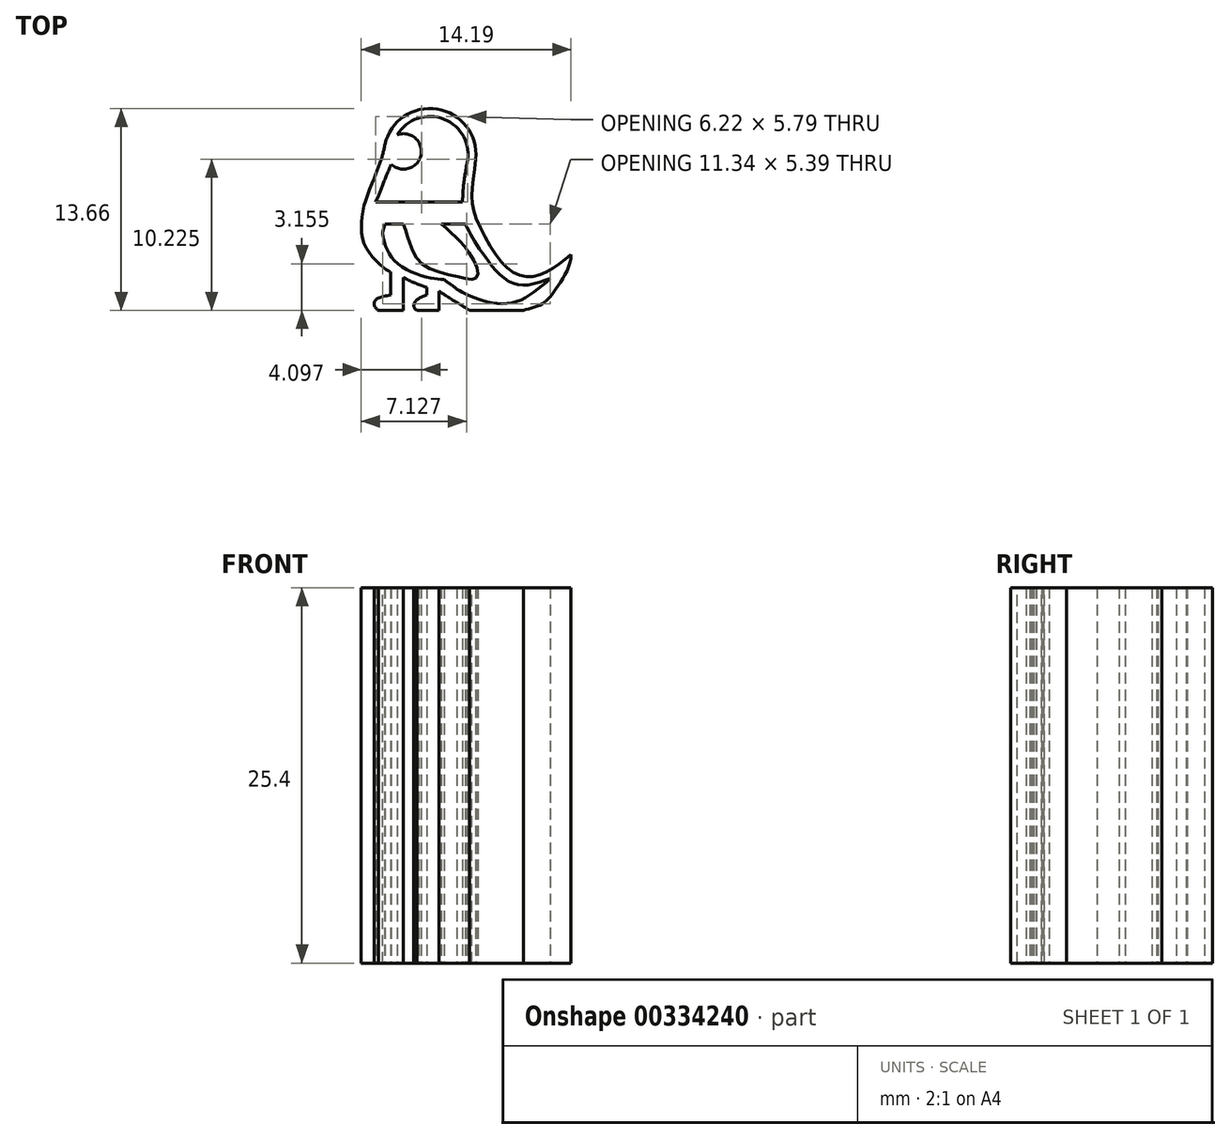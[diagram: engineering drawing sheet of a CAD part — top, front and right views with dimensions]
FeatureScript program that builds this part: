
annotation { "Feature Type Name" : "Feature", "Feature Type Description" : "" }
export const myFeature = defineFeature(function(context is Context, id is Id, definition is map)
    precondition{}
    {
        {
            var Q0;
            Q0=qCreatedBy(makeId("Top.planeOp"),FACE);
            var sketch = newSketch(context, id + "F0", { "sketchPlane" : qUnion([Q0])});
            skArc(sketch, "E0", {"start": v(-20.34, 35.83) * mm, "mid": v(-22.96, 39.22) * mm, "end": v(-26.5, 36.8) * mm});
            skLineSegment(sketch, "E1.left", {"start": v(-26.1, 28.2) * mm, "end": v(-26.1, 26.63) * mm});
            skLineSegment(sketch, "E1.right", {"start": v(-25.25, 27.82) * mm, "end": v(-25.25, 26.63) * mm});
            skFitSpline(sketch, "E2", {"points": [v(-26.1, 26.63) * mm, v(-27.1, 26.32) * mm, v(-27.2, 25.9) * mm, v(-26.93, 25.6) * mm], "startDerivative": vector(-2.75, -0.43) * mm, "endDerivative": vector(1.25, -0.98) * mm});
            skFitSpline(sketch, "E3", {"points": [v(-25.25, 26.63) * mm, v(-25.25, 25.77) * mm], "startDerivative": vector(0, -0.86) * mm, "endDerivative": vector(0, -0.86) * mm});
            skLineSegment(sketch, "E4", {"start": v(-26.93, 25.6) * mm, "end": v(-25.25, 25.6) * mm});
            skLineSegment(sketch, "E5", {"start": v(-25.25, 25.77) * mm, "end": v(-25.25, 25.6) * mm});
            skFitSpline(sketch, "E6", {"points": [v(-25.25, 27.82) * mm, v(-24.64, 27.52) * mm, v(-24.18, 27.33) * mm], "startDerivative": vector(1.23, -0.6) * mm, "endDerivative": vector(0.89, -0.38) * mm});
            skFitSpline(sketch, "E7", {"points": [v(-24.18, 27.33) * mm, v(-23.67, 27.16) * mm], "startDerivative": vector(0.51, -0.17) * mm, "endDerivative": vector(0.51, -0.17) * mm});
            skLineSegment(sketch, "E8.left", {"start": v(-23.67, 27.16) * mm, "end": v(-23.67, 26.63) * mm});
            skLineSegment(sketch, "E8.right", {"start": v(-22.82, 26.9) * mm, "end": v(-22.82, 26.63) * mm});
            skFitSpline(sketch, "E9", {"points": [v(-23.67, 26.63) * mm, v(-24.18, 26.4) * mm, v(-24.48, 26.12) * mm, v(-24.51, 25.8) * mm, v(-24.32, 25.6) * mm], "startDerivative": vector(-1.8, -0.7) * mm, "endDerivative": vector(1.18, -0.76) * mm});
            skLineSegment(sketch, "E10", {"start": v(-24.32, 25.6) * mm, "end": v(-22.82, 25.6) * mm});
            skLineSegment(sketch, "E11", {"start": v(-22.82, 26.63) * mm, "end": v(-22.82, 25.6) * mm});
            skLineSegment(sketch, "E12", {"start": v(-26.5, 36.8) * mm, "end": v(-30.17, 36.8) * mm});
            skLineSegment(sketch, "E13", {"start": v(-30.17, 36.8) * mm, "end": v(-27.08, 34.89) * mm});
            skFitSpline(sketch, "E14.trimOffspring", {"points": [v(-26.5, 36.8) * mm, v(-27.79, 33.03) * mm, v(-27.66, 29.66) * mm, v(-26.14, 28.2) * mm, v(-26.1, 28.2) * mm], "startDerivative": vector(-1.27, -9.96) * mm, "endDerivative": vector(0.77, 0.4) * mm});
            skArc(sketch, "E15", {"start": v(-20.93, 35.55) * mm, "mid": v(-22.48, 38.52) * mm, "end": v(-25.65, 37.46) * mm});
            skPoint(sketch, "E16.orphan", {"position": v(-22.82, 27.2) * mm});
            skFitSpline(sketch, "E17", {"points": [v(-20.93, 35.55) * mm, v(-21.22, 33.37) * mm, v(-20.95, 31.12) * mm, v(-19.9, 28.8) * mm], "startDerivative": vector(-1.22, -6.7) * mm, "endDerivative": vector(3.45, -6.61) * mm});
            skPoint(sketch, "E18.0.internal.orphan", {"position": v(-26.02, 36.18) * mm});
            skLineSegment(sketch, "E19.bottom", {"start": v(-26.43, 32.92) * mm, "end": v(-25.25, 32.92) * mm});
            skLineSegment(sketch, "E20.bottom", {"start": v(-21.23, 32.92) * mm, "end": v(-22.67, 32.92) * mm});
            skLineSegment(sketch, "E21", {"start": v(-25.25, 32.92) * mm, "end": v(-22.67, 32.92) * mm});
            skLineSegment(sketch, "E22", {"start": v(-26.49, 32.43) * mm, "end": v(-26.54, 32.42) * mm});
            skLineSegment(sketch, "E23", {"start": v(-26.49, 31.44) * mm, "end": v(-25.25, 31.44) * mm});
            skLineSegment(sketch, "E24", {"start": v(-21.03, 31.44) * mm, "end": v(-22.67, 31.44) * mm});
            skFitSpline(sketch, "E25", {"points": [v(-26.49, 31.44) * mm, v(-26.63, 30.65) * mm, v(-26.35, 29.74) * mm, v(-25.31, 28.52) * mm, v(-23.39, 27.78) * mm, v(-22.5, 27.7) * mm], "startDerivative": vector(-2.58, -9.76) * mm, "endDerivative": vector(4.96, 0.13) * mm});
            skFitSpline(sketch, "E26", {"points": [v(-26.05, 35.48) * mm, v(-26.6, 34.2) * mm, v(-26.93, 33.33) * mm], "startDerivative": vector(-1.05, -2.46) * mm, "endDerivative": vector(-0.68, -1.83) * mm});
            skFitSpline(sketch, "E27", {"points": [v(-25.25, 31.44) * mm, v(-24.83, 30.24) * mm, v(-23.96, 28.72) * mm, v(-21.64, 27.88) * mm, v(-20.42, 27.73) * mm, v(-20.2, 28.22) * mm, v(-21.03, 29.82) * mm, v(-21.8, 30.62) * mm, v(-22.67, 31.44) * mm], "startDerivative": vector(4.24, -10.15) * mm, "endDerivative": vector(-8.23, 6.32) * mm});
            skFitSpline(sketch, "E28", {"points": [v(-20.34, 35.83) * mm, v(-20.6, 33.43) * mm, v(-20.34, 31.9) * mm, v(-19, 29.37) * mm, v(-17.69, 28.1) * mm, v(-16.46, 27.88) * mm, v(-15.13, 28.44) * mm, v(-13.9, 29.37) * mm], "startDerivative": vector(-1.94, -16.25) * mm, "endDerivative": vector(8.98, 7.43) * mm});
            skFitSpline(sketch, "E29", {"points": [v(-17.12, 25.6) * mm, v(-15.9, 26) * mm, v(-15, 26.94) * mm, v(-13.9, 29.37) * mm], "startDerivative": vector(4.07, 1.12) * mm, "endDerivative": vector(-0.04, 6.39) * mm});
            skArc(sketch, "E30", {"start": v(-26.06, 35.48) * mm, "mid": v(-24.05, 36.1) * mm, "end": v(-25.65, 37.46) * mm});
            skFitSpline(sketch, "E31", {"points": [v(-22.5, 27.7) * mm, v(-21.6, 27.02) * mm], "startDerivative": vector(0.9, -0.84) * mm, "endDerivative": vector(0.9, -0.84) * mm});
            skFitSpline(sketch, "E32", {"points": [v(-22.82, 26.9) * mm, v(-22.02, 26.37) * mm, v(-20.75, 25.6) * mm], "startDerivative": vector(1.7, -1.13) * mm, "endDerivative": vector(2.42, -1.46) * mm});
            skFitSpline(sketch, "E33", {"points": [v(-20.75, 25.6) * mm, v(-20.34, 25.6) * mm, v(-17.12, 25.6) * mm], "startDerivative": vector(1.19, 0) * mm, "endDerivative": vector(5.4, 0) * mm});
            skLineSegment(sketch, "E34", {"start": v(-26.93, 33.33) * mm, "end": v(-27.1, 32.92) * mm});
            skLineSegment(sketch, "E35", {"start": v(-27.1, 32.92) * mm, "end": v(-26.43, 32.92) * mm});
            skPoint(sketch, "E36.5.internal.snap0", {"position": v(-40.87, 34.02) * mm});
            skFitSpline(sketch, "E37", {"points": [v(-21.03, 31.44) * mm, v(-20.58, 30.54) * mm, v(-19.96, 29.57) * mm, v(-18.7, 28) * mm, v(-17.22, 27.3) * mm, v(-15.3, 27.75) * mm], "startDerivative": vector(2.65, -5.66) * mm, "endDerivative": vector(8.76, 3.2) * mm});
            skFitSpline(sketch, "E38", {"points": [v(-21.6, 27.02) * mm, v(-20.5, 26.47) * mm, v(-17.92, 26.1) * mm, v(-15.3, 27.75) * mm], "startDerivative": vector(3.83, -2.2) * mm, "endDerivative": vector(6.34, 5.6) * mm});
            skSolve(sketch);
        }
        {
            var Q0;
            Q0=makeQuery(id+"F0.imprint","IMPRINT",FACE,{"disambiguationData":[TD([[makeQuery(id+"F0.imprint","IMPRINT",EDGE,{"derivedFrom":sQuery(id+"F0.wireOp",EDGE,"E0")}),1.0]])]});
            extrude(context, id + "F1", {"entities" : qUnion([Q0]), "depth" : 25.4 * mm});
        }
    });
